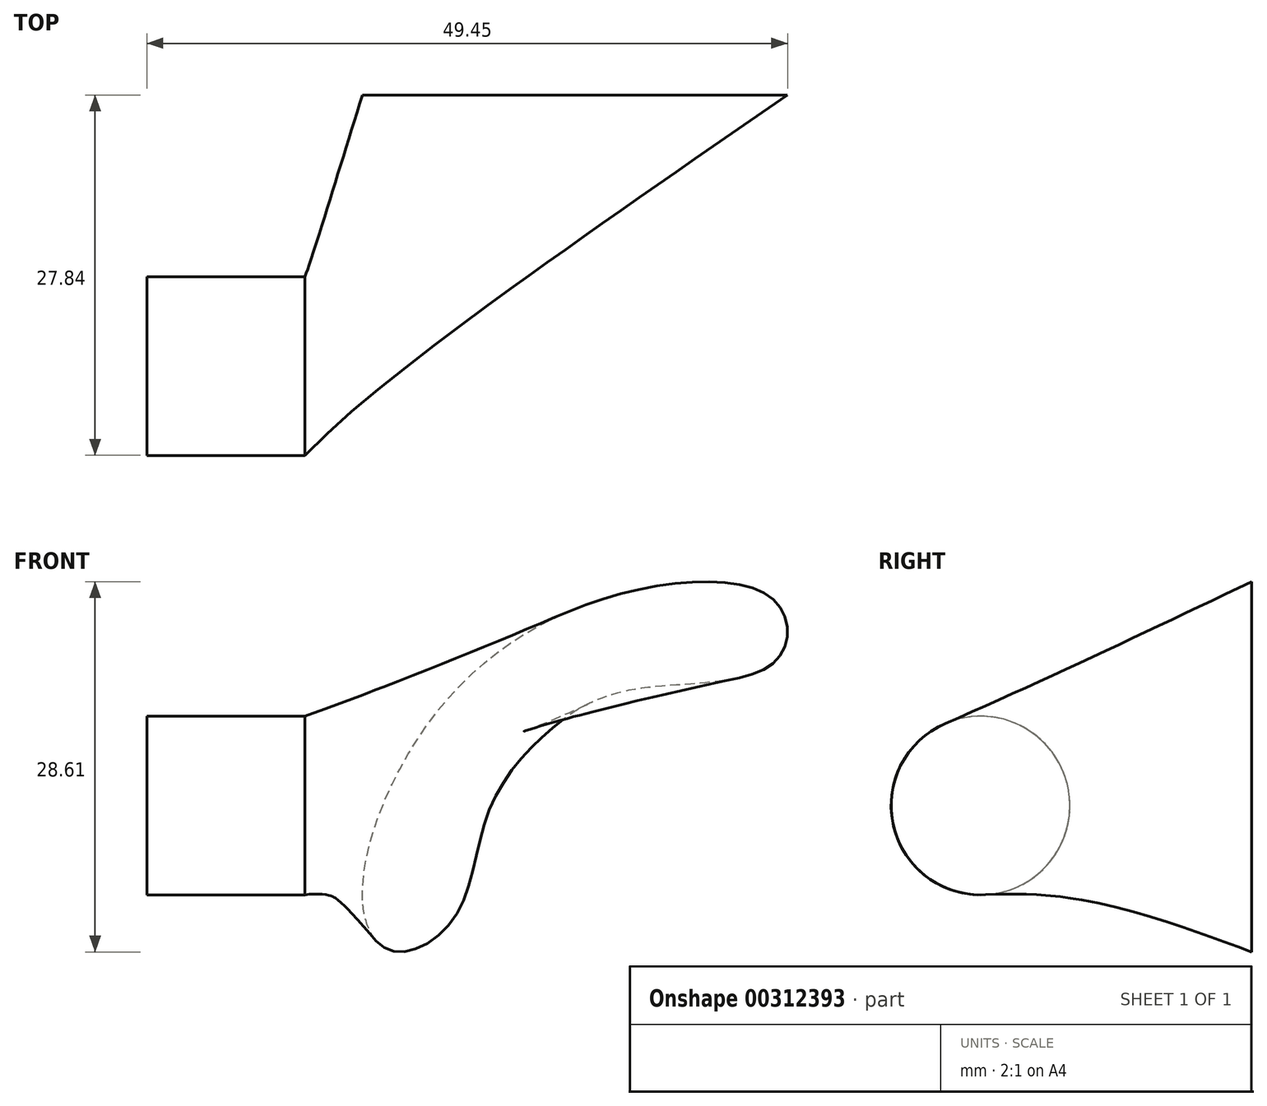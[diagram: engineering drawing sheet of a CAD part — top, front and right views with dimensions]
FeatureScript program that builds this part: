
annotation { "Feature Type Name" : "Feature", "Feature Type Description" : "" }
export const myFeature = defineFeature(function(context is Context, id is Id, definition is map)
    precondition{}
    {
        {
            var Q0;
            Q0=qCreatedBy(makeId("Front.planeOp"),FACE);
            var sketch = newSketch(context, id + "F0", { "sketchPlane" : qUnion([Q0])});
            skLineSegment(sketch, "E0.bottom", {"start": v(0, 0) * mm, "end": v(73.47, 0) * mm});
            skLineSegment(sketch, "E0.top", {"start": v(0, 35.83) * mm, "end": v(73.47, 35.83) * mm});
            skLineSegment(sketch, "E0.left", {"start": v(0, 0) * mm, "end": v(0, 35.83) * mm});
            skLineSegment(sketch, "E0.right", {"start": v(73.47, 0) * mm, "end": v(73.47, 35.83) * mm});
            skFitSpline(sketch, "E1", {"points": [v(4.46, 7.45) * mm, v(9.71, 21.38) * mm, v(23.38, 30.84) * mm, v(36.26, 30.58) * mm, v(36.26, 25.85) * mm, v(25.48, 23.75) * mm, v(18.91, 20.6) * mm, v(14.18, 14.28) * mm, v(11.55, 6.14) * mm, v(6.82, 3.5) * mm, v(4.46, 7.45) * mm]});
            skSolve(sketch);
        }
        {
            var Q0;
            Q0=qCreatedBy(makeId("Right.planeOp"),FACE);
            var sketch = newSketch(context, id + "F1", { "sketchPlane" : qUnion([Q0])});
            skCircle(sketch, "E2", {"center": v(-20.94, 14.77) * mm, "radius": 6.9 * mm});
            skSolve(sketch);
        }
        {
            var Q0;
            Q0=makeQuery(id+"F1.imprint","IMPRINT",FACE,{"disambiguationData":[TD([[makeQuery(id+"F1.imprint","IMPRINT",EDGE,{"derivedFrom":sQuery(id+"F1.wireOp",EDGE,"E2")}),1.0]])]});
            extrude(context, id + "F2", {"entities" : qUnion([Q0]), "oppositeDirection" : true, "depth" : 12.2 * mm});
        }
        {
            var Q0;
            Q0=makeQuery(id+"F0.imprint","IMPRINT",FACE,{"disambiguationData":[TD([[makeQuery(id+"F0.imprint","IMPRINT",EDGE,{"derivedFrom":sQuery(id+"F0.wireOp",EDGE,"E1")}),-1.0]])]});
            var Q1;
            Q1=makeQuery(id+"F2.opExtrude","CAP_FACE",FACE,{"disambiguationData":[OSD([sQuery(id+"F1.wireOp",EDGE,"E2")])],"isStart":true});
            loft(context, id + "F3", {"sheetProfilesArray" : [{ "sheetProfileEntities" : qUnion([Q0]) }, { "sheetProfileEntities" : qUnion([Q1]) }]});
        }
    });
